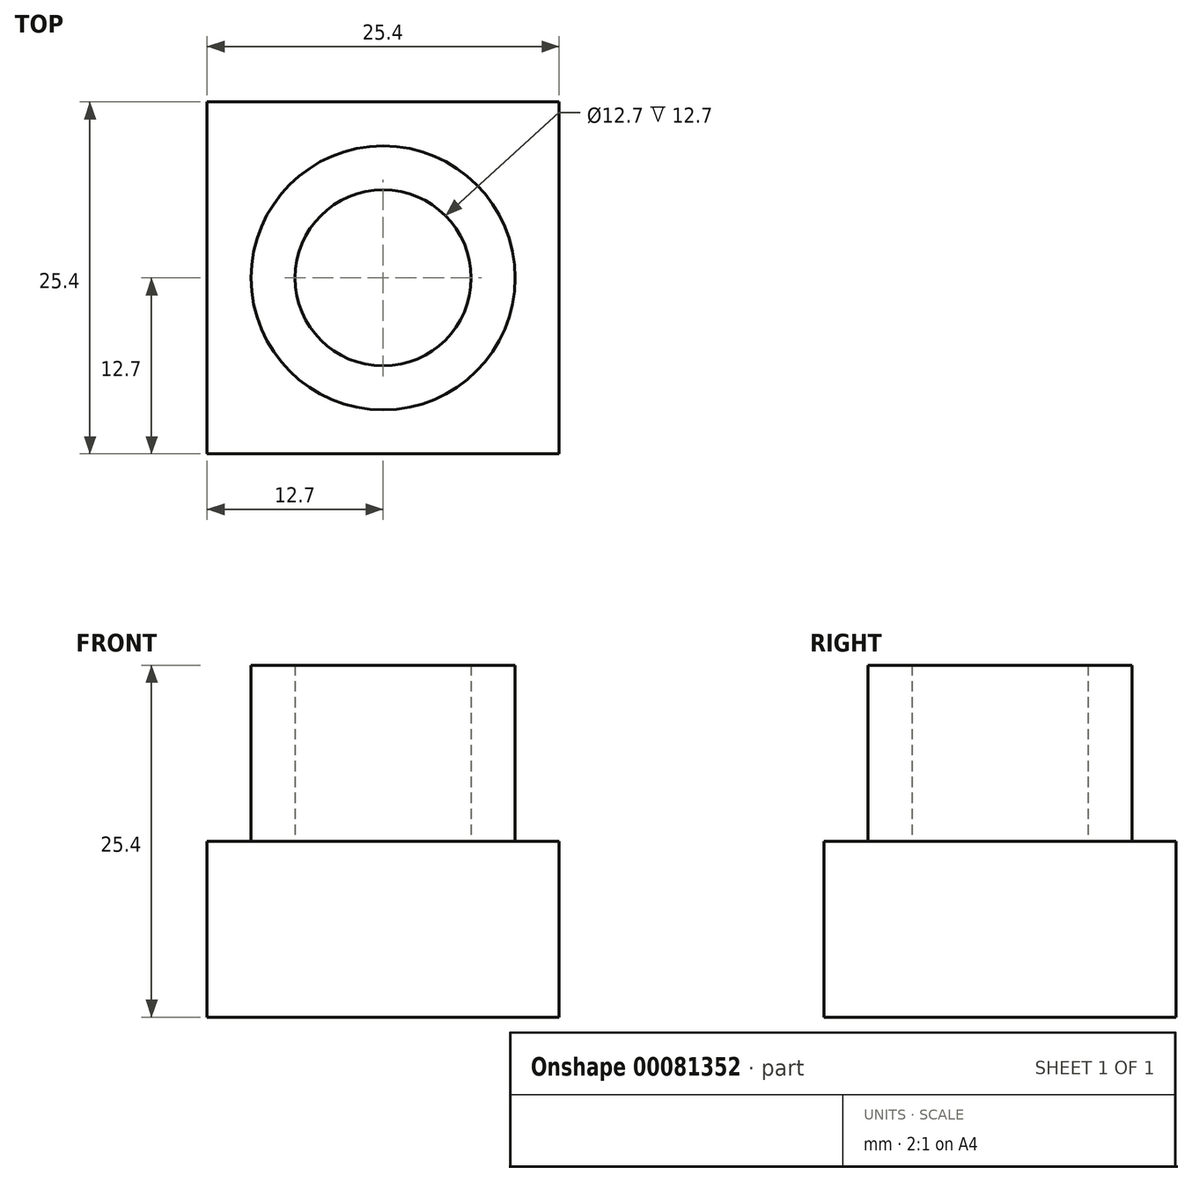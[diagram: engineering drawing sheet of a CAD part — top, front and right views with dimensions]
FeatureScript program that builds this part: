
annotation { "Feature Type Name" : "Feature", "Feature Type Description" : "" }
export const myFeature = defineFeature(function(context is Context, id is Id, definition is map)
    precondition{}
    {
        {
            var Q0;
            Q0=qCreatedBy(makeId("Top.planeOp"),FACE);
            var sketch = newSketch(context, id + "F0", { "sketchPlane" : qUnion([Q0])});
            skLineSegment(sketch, "E0.bottom", {"start": v(-12.7, 12.7) * mm, "end": v(12.7, 12.7) * mm});
            skLineSegment(sketch, "E0.top", {"start": v(-12.7, -12.7) * mm, "end": v(12.7, -12.7) * mm});
            skLineSegment(sketch, "E0.left", {"start": v(-12.7, 12.7) * mm, "end": v(-12.7, -12.7) * mm});
            skLineSegment(sketch, "E0.right", {"start": v(12.7, 12.7) * mm, "end": v(12.7, -12.7) * mm});
            skPoint(sketch, "E0.middle", {"position": v(0, 0) * mm});
            skSolve(sketch);
        }
        {
            var Q0;
            Q0=makeQuery(id+"F0.imprint","IMPRINT",FACE,{"disambiguationData":[TD([[makeQuery(id+"F0.imprint","IMPRINT",EDGE,{"derivedFrom":sQuery(id+"F0.wireOp",EDGE,"E0.bottom")}),-1.0]])]});
            extrude(context, id + "F1", {"entities" : qUnion([Q0]), "depth" : 12.7 * mm});
        }
        {
            var Q0;
            Q0=makeQuery(id+"F1.opExtrude","CAP_FACE",FACE,{"disambiguationData":[OSD([sQuery(id+"F0.wireOp",EDGE,"E0.bottom"),sQuery(id+"F0.wireOp",EDGE,"E0.top"),sQuery(id+"F0.wireOp",EDGE,"E0.left"),sQuery(id+"F0.wireOp",EDGE,"E0.right")])],"isStart":false});
            var sketch = newSketch(context, id + "F2", { "sketchPlane" : qUnion([Q0])});
            skCircle(sketch, "E1", {"center": v(0, 0) * mm, "radius": 9.53 * mm});
            skCircle(sketch, "E2", {"center": v(0, 0) * mm, "radius": 6.35 * mm});
            skSolve(sketch);
        }
        {
            var Q0;
            Q0=makeQuery(id+"F2.imprint","IMPRINT",FACE,{"disambiguationData":[TD([[makeQuery(id+"F2.imprint","IMPRINT",EDGE,{"derivedFrom":sQuery(id+"F2.wireOp",EDGE,"E1")}),1.0]])]});
            extrude(context, id + "F3", {"entities" : qUnion([Q0]), "operationType" : NewBodyOperationType.ADD, "depth" : 12.7 * mm});
        }
    });
